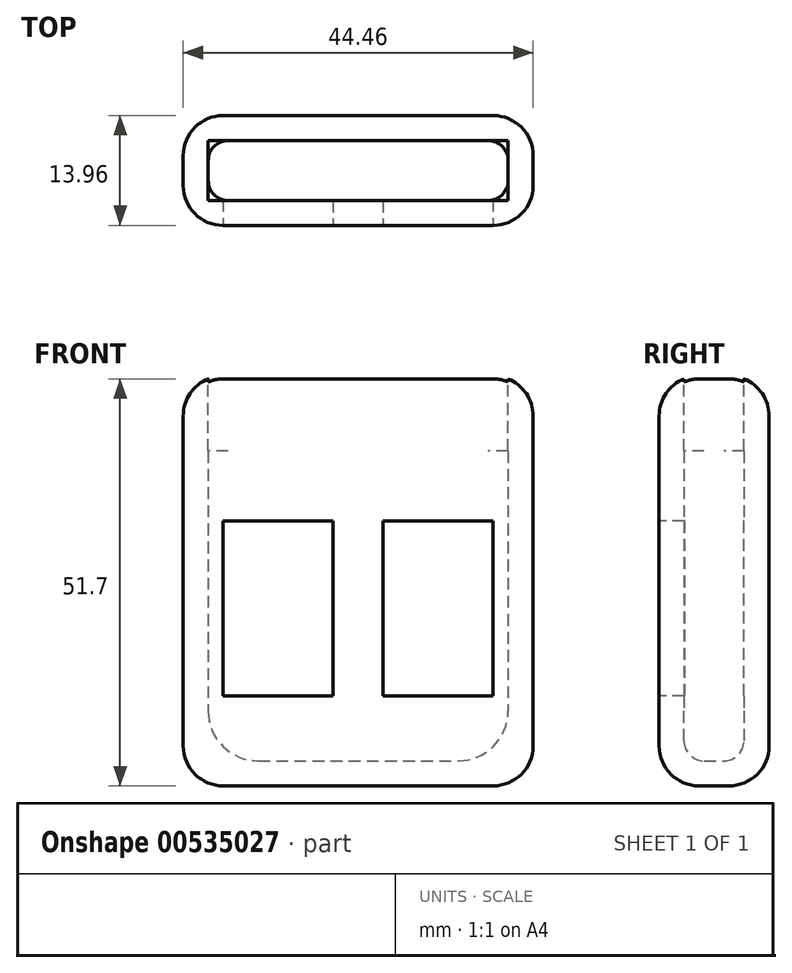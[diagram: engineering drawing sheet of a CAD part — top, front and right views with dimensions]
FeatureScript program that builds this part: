
annotation { "Feature Type Name" : "Feature", "Feature Type Description" : "" }
export const myFeature = defineFeature(function(context is Context, id is Id, definition is map)
    precondition{}
    {
        {
            var Q0;
            Q0=qCreatedBy(makeId("Front.planeOp"),FACE);
            var sketch = newSketch(context, id + "F0", { "sketchPlane" : qUnion([Q0])});
            skLineSegment(sketch, "E0.bottom", {"start": v(-12.7, 22.86) * mm, "end": v(12.7, 22.86) * mm});
            skLineSegment(sketch, "E0.top", {"start": v(-12.7, -22.86) * mm, "end": v(12.7, -22.86) * mm});
            skLineSegment(sketch, "E0.left", {"start": v(-19.05, 16.51) * mm, "end": v(-19.05, -16.5) * mm});
            skLineSegment(sketch, "E0.right", {"start": v(19.05, 16.51) * mm, "end": v(19.05, -16.51) * mm});
            skPoint(sketch, "E1.visualSharp", {"position": v(-19.05, 22.86) * mm});
            skArc(sketch, "E1.filletArc", {"start": v(-12.7, 22.86) * mm, "mid": v(-17.2, 21) * mm, "end": v(-19.05, 16.51) * mm});
            skPoint(sketch, "E2.visualSharp", {"position": v(19.05, 22.86) * mm});
            skArc(sketch, "E2.filletArc", {"start": v(19.05, 16.51) * mm, "mid": v(17.2, 21) * mm, "end": v(12.7, 22.86) * mm});
            skPoint(sketch, "E3.visualSharp", {"position": v(19.05, -22.86) * mm});
            skArc(sketch, "E3.filletArc", {"start": v(12.7, -22.86) * mm, "mid": v(17.2, -21) * mm, "end": v(19.05, -16.51) * mm});
            skPoint(sketch, "E4.visualSharp", {"position": v(-19.05, -22.86) * mm});
            skArc(sketch, "E4.filletArc", {"start": v(-19.05, -16.5) * mm, "mid": v(-17.2, -21) * mm, "end": v(-12.7, -22.86) * mm});
            skLineSegment(sketch, "E5", {"start": v(0, 22.86) * mm, "end": v(0, 0) * mm, "construction": true});
            skLineSegment(sketch, "E6", {"start": v(0, 0) * mm, "end": v(19.05, 0) * mm, "construction": true});
            skSolve(sketch);
        }
        {
            var Q0;
            Q0 = qSketchRegion(id + "F0", true);
            extrude(context, id + "F1", {"entities" : qUnion([Q0]), "depth" : 7.62 * mm, "offsetDistance" : 25.4 * mm});
        }
        {
            var Q0;
            Q0=makeQuery(id+"F1.opExtrude","CAP_EDGE",EDGE,{"disambiguationData":[OSD([sQuery(id+"F0.wireOp",EDGE,"E0.right")])],"isStart":false});
            var Q1;
            Q1=makeQuery(id+"F1.opExtrude","CAP_EDGE",EDGE,{"disambiguationData":[OSD([sQuery(id+"F0.wireOp",EDGE,"E0.right")])],"isStart":true});
            fillet(context, id + "F2", {"entities" : qUnion([Q0, Q1]), "radius" : 2.54 * mm, "tangentPropagation" : true, "allowEdgeOverflow" : false});
        }
        {
            var Q0;
            Q0=makeQuery(id+"F1.opExtrude","CAP_FACE",FACE,{"disambiguationData":[OSD([sQuery(id+"F0.wireOp",EDGE,"E0.bottom"),sQuery(id+"F0.wireOp",EDGE,"E0.top"),sQuery(id+"F0.wireOp",EDGE,"E0.left"),sQuery(id+"F0.wireOp",EDGE,"E0.right"),sQuery(id+"F0.wireOp",EDGE,"E1.filletArc"),sQuery(id+"F0.wireOp",EDGE,"E2.filletArc"),sQuery(id+"F0.wireOp",EDGE,"E3.filletArc"),sQuery(id+"F0.wireOp",EDGE,"E4.filletArc")])],"isStart":false});
            var sketch = newSketch(context, id + "F3", { "sketchPlane" : qUnion([Q0])});
            skLineSegment(sketch, "E7.bottom", {"start": v(-22.22, 26.03) * mm, "end": v(22.22, 26.04) * mm});
            skLineSegment(sketch, "E7.left", {"start": v(-22.22, 26.03) * mm, "end": v(-22.22, -26.04) * mm});
            skLineSegment(sketch, "E7.right", {"start": v(22.23, 26.04) * mm, "end": v(22.23, -26.04) * mm});
            skLineSegment(sketch, "E8.top", {"start": v(-22.22, -26.04) * mm, "end": v(22.23, -26.04) * mm});
            skLineSegment(sketch, "E9", {"start": v(0, 26.04) * mm, "end": v(0, 0) * mm, "construction": true});
            skLineSegment(sketch, "E10", {"start": v(0, 0) * mm, "end": v(22.23, 0) * mm, "construction": true});
            skSolve(sketch);
        }
        {
            var Q0;
            Q0 = qSketchRegion(id + "F3", true);
            extrude(context, id + "F4", {"entities" : qUnion([Q0]), "depth" : 3.17 * mm, "offsetDistance" : 25.4 * mm, "hasSecondDirection" : true, "secondDirectionOppositeDirection" : true, "secondDirectionDepth" : 10.8 * mm});
        }
        {
            var Q0;
            Q0=makeQuery(id+"F4.opExtrude","CAP_FACE",FACE,{"disambiguationData":[OSD([sQuery(id+"F3.wireOp",EDGE,"E7.bottom"),sQuery(id+"F3.wireOp",EDGE,"E7.left"),sQuery(id+"F3.wireOp",EDGE,"E7.right"),sQuery(id+"F3.wireOp",EDGE,"E8.top")])],"isStart":false});
            var Q1;
            Q1=makeQuery(id+"F4.opExtrude","CAP_FACE",FACE,{"disambiguationData":[OSD([sQuery(id+"F3.wireOp",EDGE,"E7.bottom"),sQuery(id+"F3.wireOp",EDGE,"E7.left"),sQuery(id+"F3.wireOp",EDGE,"E7.right"),sQuery(id+"F3.wireOp",EDGE,"E8.top")])],"isStart":true});
            var Q2;
            Q2=makeQuery(id+"F4.opExtrude","SWEPT_EDGE",EDGE,{"disambiguationData":[OSD([sQuery(id+"F3.wireOp",EDGE,"E7.bottom"),sQuery(id+"F3.wireOp",EDGE,"E7.right")])]});
            var Q3;
            Q3=makeQuery(id+"F4.opExtrude","SWEPT_EDGE",EDGE,{"disambiguationData":[OSD([sQuery(id+"F3.wireOp",EDGE,"E7.bottom"),sQuery(id+"F3.wireOp",EDGE,"E7.left")])]});
            var Q4;
            Q4=makeQuery(id+"F4.opExtrude","SWEPT_EDGE",EDGE,{"disambiguationData":[OSD([sQuery(id+"F3.wireOp",EDGE,"E7.left"),sQuery(id+"F3.wireOp",EDGE,"E8.top")])]});
            var Q5;
            Q5=makeQuery(id+"F4.opExtrude","SWEPT_EDGE",EDGE,{"disambiguationData":[OSD([sQuery(id+"F3.wireOp",EDGE,"E7.right"),sQuery(id+"F3.wireOp",EDGE,"E8.top")])]});
            fillet(context, id + "F5", {"entities" : qUnion([Q0, Q1, Q2, Q3, Q4, Q5]), "radius" : 5.08 * mm, "tangentPropagation" : true, "allowEdgeOverflow" : false});
        }
        {
            var Q0;
            Q0=makeQuery(id+"F1.opExtrude","SWEPT_BODY",BODY,{"disambiguationData":[OSD([sQuery(id+"F0.wireOp",EDGE,"E0.bottom"),sQuery(id+"F0.wireOp",EDGE,"E0.top"),sQuery(id+"F0.wireOp",EDGE,"E0.left"),sQuery(id+"F0.wireOp",EDGE,"E0.right"),sQuery(id+"F0.wireOp",EDGE,"E1.filletArc"),sQuery(id+"F0.wireOp",EDGE,"E2.filletArc"),sQuery(id+"F0.wireOp",EDGE,"E3.filletArc"),sQuery(id+"F0.wireOp",EDGE,"E4.filletArc")])]});
            var Q1;
            Q1=makeQuery(id+"F4.opExtrude","SWEPT_BODY",BODY,{"disambiguationData":[OSD([sQuery(id+"F3.wireOp",EDGE,"E7.bottom"),sQuery(id+"F3.wireOp",EDGE,"E7.left"),sQuery(id+"F3.wireOp",EDGE,"E7.right"),sQuery(id+"F3.wireOp",EDGE,"E8.top")])]});
            booleanBodies(context, id + "F6", {"operationType" : BooleanOperationType.SUBTRACTION, "tools" : qUnion([Q0]), "targets" : qUnion([Q1])});
        }
        {
            var Q0;
            Q0=makeQuery(id+"F4.opExtrude","SWEPT_FACE",FACE,{"disambiguationData":[OSD([sQuery(id+"F3.wireOp",EDGE,"E7.bottom")])]});
            var sketch = newSketch(context, id + "F7", { "sketchPlane" : qUnion([Q0])});
            skLineSegment(sketch, "E11.bottom", {"start": v(19.05, 0) * mm, "end": v(-19.05, 0) * mm});
            skLineSegment(sketch, "E11.top", {"start": v(19.05, -7.62) * mm, "end": v(-19.05, -7.62) * mm});
            skLineSegment(sketch, "E11.left", {"start": v(19.05, 0) * mm, "end": v(19.05, -7.62) * mm});
            skLineSegment(sketch, "E11.right", {"start": v(-19.05, 0) * mm, "end": v(-19.05, -7.62) * mm});
            skSolve(sketch);
        }
        {
            var Q0;
            Q0 = qSketchRegion(id + "F7", true);
            var Q1;
            {var subQ0=sQuery(id+"F0.wireOp",EDGE,"E1.filletArc");var subQ1=sQuery(id+"F0.wireOp",EDGE,"E0.left");Q1=makeQuery(id+"F6.opBoolean","COPY",VERTEX,{"derivedFrom":makeQuery(id+"F2.opFillet","BLEND_VERTEX",VERTEX,{"blendedFrom":[makeQuery(id+"F1.opExtrude","CAP_EDGE",EDGE,{"disambiguationData":[OSD([subQ1])],"isStart":true}),makeQuery(id+"F1.opExtrude","CAP_EDGE",EDGE,{"disambiguationData":[OSD([subQ0])],"isStart":true}),makeQuery(id+"F1.opExtrude","SWEPT_FACE",FACE,{"disambiguationData":[OSD([subQ1])]}),makeQuery(id+"F1.opExtrude","SWEPT_FACE",FACE,{"disambiguationData":[OSD([subQ0])]})],"blendedInto":[makeQuery(id+"F1.opExtrude","SWEPT_FACE",FACE,{"disambiguationData":[OSD([subQ1])]}),makeQuery(id+"F1.opExtrude","SWEPT_FACE",FACE,{"disambiguationData":[OSD([subQ0])]})]})});}
            extrude(context, id + "F8", {"entities" : qUnion([Q0]), "operationType" : NewBodyOperationType.REMOVE, "endBound" : BoundingType.UP_TO_VERTEX, "oppositeDirection" : true, "depth" : 25.4 * mm, "endBoundEntityVertex" : qUnion([Q1]), "offsetDistance" : 25.4 * mm});
        }
        {
            var Q0;
            Q0=makeQuery(id+"F4.opExtrude","CAP_FACE",FACE,{"disambiguationData":[OSD([sQuery(id+"F3.wireOp",EDGE,"E7.bottom"),sQuery(id+"F3.wireOp",EDGE,"E7.left"),sQuery(id+"F3.wireOp",EDGE,"E7.right"),sQuery(id+"F3.wireOp",EDGE,"E8.top")])],"isStart":false});
            var sketch = newSketch(context, id + "F9", { "sketchPlane" : qUnion([Q0])});
            skLineSegment(sketch, "E12.bottom", {"start": v(-17.14, 7.62) * mm, "end": v(-3.18, 7.62) * mm});
            skLineSegment(sketch, "E12.top", {"start": v(-17.14, -14.6) * mm, "end": v(-3.17, -14.6) * mm});
            skLineSegment(sketch, "E12.left", {"start": v(-17.14, 7.62) * mm, "end": v(-17.14, -14.6) * mm});
            skLineSegment(sketch, "E12.right", {"start": v(-3.18, 7.62) * mm, "end": v(-3.17, -14.6) * mm});
            skLineSegment(sketch, "E13.bottom", {"start": v(3.17, 7.62) * mm, "end": v(17.15, 7.62) * mm});
            skLineSegment(sketch, "E13.top", {"start": v(3.18, -14.6) * mm, "end": v(17.15, -14.6) * mm});
            skLineSegment(sketch, "E13.left", {"start": v(3.17, 7.62) * mm, "end": v(3.18, -14.6) * mm});
            skLineSegment(sketch, "E13.right", {"start": v(17.15, 7.62) * mm, "end": v(17.15, -14.6) * mm});
            skSolve(sketch);
        }
        {
            var Q0;
            Q0 = qSketchRegion(id + "F9", true);
            var Q1;
            Q1=makeQuery(id+"F8.boolean.opBoolean","MERGE",FACE,{"derivedFrom":[makeQuery(id+"F6.opBoolean","COPY",FACE,{"derivedFrom":makeQuery(id+"F1.opExtrude","CAP_FACE",FACE,{"disambiguationData":[OSD([sQuery(id+"F0.wireOp",EDGE,"E0.bottom"),sQuery(id+"F0.wireOp",EDGE,"E0.top"),sQuery(id+"F0.wireOp",EDGE,"E0.left"),sQuery(id+"F0.wireOp",EDGE,"E0.right"),sQuery(id+"F0.wireOp",EDGE,"E1.filletArc"),sQuery(id+"F0.wireOp",EDGE,"E2.filletArc"),sQuery(id+"F0.wireOp",EDGE,"E3.filletArc"),sQuery(id+"F0.wireOp",EDGE,"E4.filletArc")])],"isStart":true})}),makeQuery(id+"F8.opExtrude","SWEPT_FACE",FACE,{"disambiguationData":[OSD([sQuery(id+"F7.wireOp",EDGE,"E11.bottom")])]})]});
            extrude(context, id + "F10", {"entities" : qUnion([Q0]), "operationType" : NewBodyOperationType.REMOVE, "endBound" : BoundingType.UP_TO_SURFACE, "oppositeDirection" : true, "depth" : 25.4 * mm, "endBoundEntityFace" : qUnion([Q1]), "offsetDistance" : 25.4 * mm});
        }
    });
